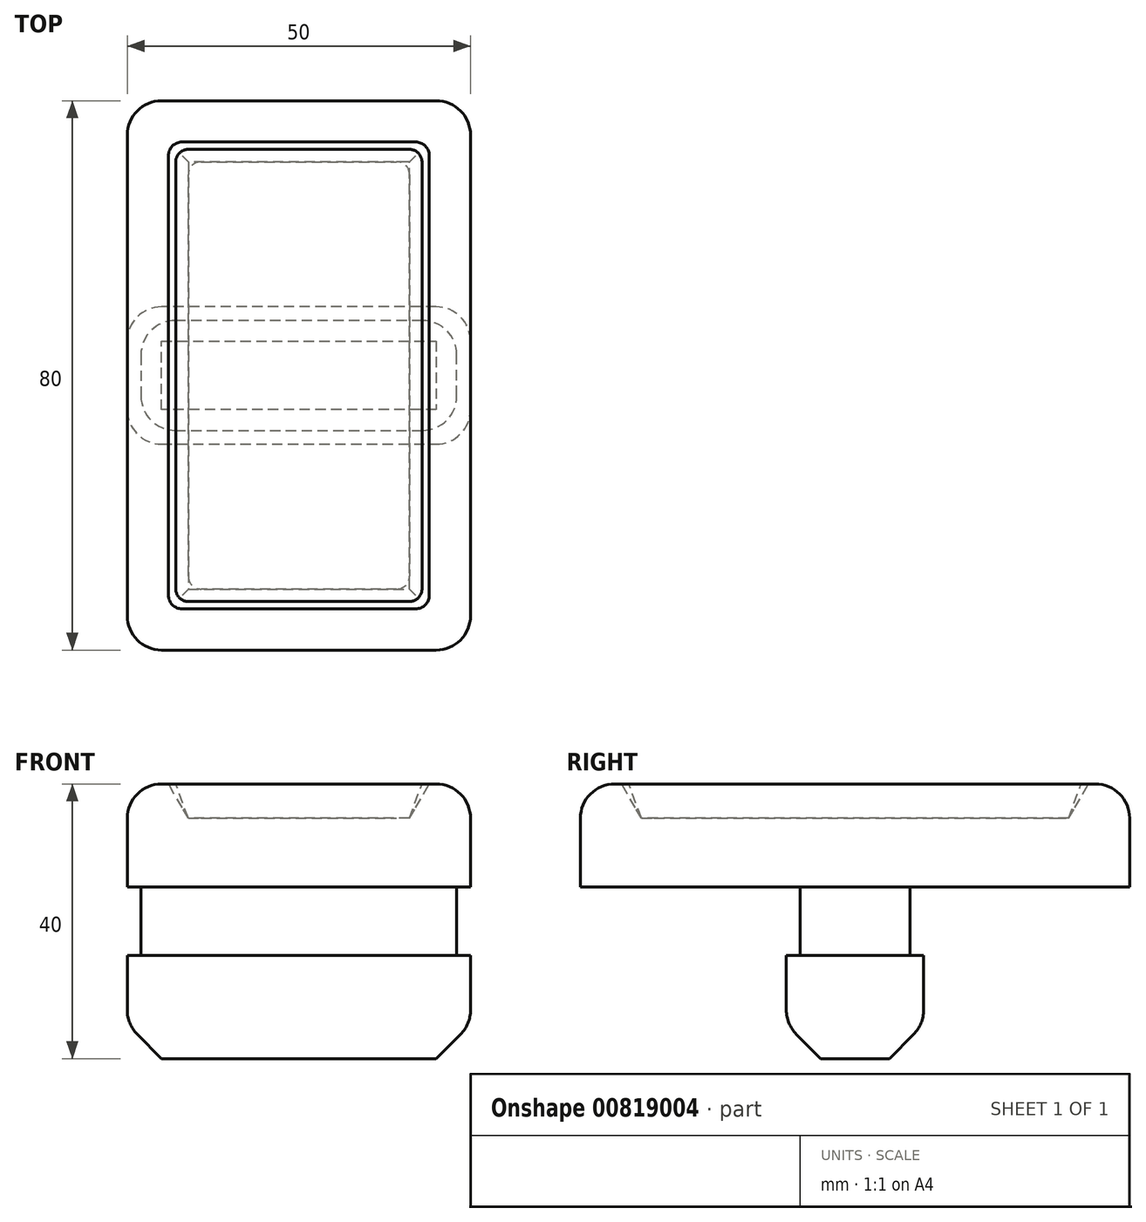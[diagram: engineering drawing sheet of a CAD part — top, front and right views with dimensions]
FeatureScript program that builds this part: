
annotation { "Feature Type Name" : "Feature", "Feature Type Description" : "" }
export const myFeature = defineFeature(function(context is Context, id is Id, definition is map)
    precondition{}
    {
        {
            var Q0;
            Q0=qCreatedBy(makeId("Top.planeOp"),FACE);
            var sketch = newSketch(context, id + "F0", { "sketchPlane" : qUnion([Q0])});
            skLineSegment(sketch, "E0.bottom", {"start": v(25, 40) * mm, "end": v(-25, 40) * mm});
            skLineSegment(sketch, "E0.top", {"start": v(25, -40) * mm, "end": v(-25, -40) * mm});
            skLineSegment(sketch, "E0.left", {"start": v(25, 40) * mm, "end": v(25, -40) * mm});
            skLineSegment(sketch, "E0.right", {"start": v(-25, 40) * mm, "end": v(-25, -40) * mm});
            skPoint(sketch, "E0.middle", {"position": v(0, 0) * mm});
            skSolve(sketch);
        }
        {
            var Q0;
            Q0=makeQuery(id+"F0.imprint","IMPRINT",FACE,{"disambiguationData":[TD([[makeQuery(id+"F0.imprint","IMPRINT",EDGE,{"derivedFrom":sQuery(id+"F0.wireOp",EDGE,"E0.bottom")}),1.0]])]});
            extrude(context, id + "F1", {"entities" : qUnion([Q0]), "depth" : 15 * mm, "offsetDistance" : 25 * mm});
        }
        {
            var Q0;
            Q0=makeQuery(id+"F1.opExtrude","CAP_EDGE",EDGE,{"disambiguationData":[OSD([sQuery(id+"F0.wireOp",EDGE,"E0.right")])],"isStart":false});
            var Q1;
            Q1=makeQuery(id+"F1.opExtrude","CAP_EDGE",EDGE,{"disambiguationData":[OSD([sQuery(id+"F0.wireOp",EDGE,"E0.top")])],"isStart":false});
            var Q2;
            Q2=makeQuery(id+"F1.opExtrude","CAP_EDGE",EDGE,{"disambiguationData":[OSD([sQuery(id+"F0.wireOp",EDGE,"E0.left")])],"isStart":false});
            var Q3;
            Q3=makeQuery(id+"F1.opExtrude","CAP_EDGE",EDGE,{"disambiguationData":[OSD([sQuery(id+"F0.wireOp",EDGE,"E0.bottom")])],"isStart":false});
            var Q4;
            Q4=makeQuery(id+"F1.opExtrude","SWEPT_EDGE",EDGE,{"disambiguationData":[OSD([sQuery(id+"F0.wireOp",EDGE,"E0.top"),sQuery(id+"F0.wireOp",EDGE,"E0.right")])]});
            var Q5;
            Q5=makeQuery(id+"F1.opExtrude","SWEPT_EDGE",EDGE,{"disambiguationData":[OSD([sQuery(id+"F0.wireOp",EDGE,"E0.top"),sQuery(id+"F0.wireOp",EDGE,"E0.left")])]});
            var Q6;
            Q6=makeQuery(id+"F1.opExtrude","SWEPT_EDGE",EDGE,{"disambiguationData":[OSD([sQuery(id+"F0.wireOp",EDGE,"E0.bottom"),sQuery(id+"F0.wireOp",EDGE,"E0.right")])]});
            var Q7;
            Q7=makeQuery(id+"F1.opExtrude","SWEPT_EDGE",EDGE,{"disambiguationData":[OSD([sQuery(id+"F0.wireOp",EDGE,"E0.bottom"),sQuery(id+"F0.wireOp",EDGE,"E0.left")])]});
            fillet(context, id + "F2", {"entities" : qUnion([Q0, Q1, Q2, Q3, Q4, Q5, Q6, Q7]), "radius" : 5 * mm, "tangentPropagation" : true, "allowEdgeOverflow" : false});
        }
        {
            var Q0;
            Q0=makeQuery(id+"F1.opExtrude","CAP_FACE",FACE,{"disambiguationData":[OSD([sQuery(id+"F0.wireOp",EDGE,"E0.bottom"),sQuery(id+"F0.wireOp",EDGE,"E0.top"),sQuery(id+"F0.wireOp",EDGE,"E0.left"),sQuery(id+"F0.wireOp",EDGE,"E0.right")])],"isStart":true});
            var sketch = newSketch(context, id + "F3", { "sketchPlane" : qUnion([Q0])});
            skLineSegment(sketch, "E1.0", {"start": v(-23, -3) * mm, "end": v(-23, 3) * mm});
            skLineSegment(sketch, "E1.1", {"start": v(-18, 8) * mm, "end": v(18, 8) * mm});
            skLineSegment(sketch, "E1.2", {"start": v(23, 3) * mm, "end": v(23, -3) * mm});
            skLineSegment(sketch, "E1.3", {"start": v(18, -8) * mm, "end": v(-18, -8) * mm});
            skPoint(sketch, "E2.visualSharp", {"position": v(-23, 8) * mm});
            skArc(sketch, "E2.filletArc", {"start": v(-18, 8) * mm, "mid": v(-21.54, 6.54) * mm, "end": v(-23, 3) * mm});
            skPoint(sketch, "E3.visualSharp", {"position": v(23, 8) * mm});
            skArc(sketch, "E3.filletArc", {"start": v(23, 3) * mm, "mid": v(21.54, 6.54) * mm, "end": v(18, 8) * mm});
            skPoint(sketch, "E4.visualSharp", {"position": v(23, -8) * mm});
            skArc(sketch, "E4.filletArc", {"start": v(18, -8) * mm, "mid": v(21.54, -6.54) * mm, "end": v(23, -3) * mm});
            skPoint(sketch, "E5.visualSharp", {"position": v(-23, -8) * mm});
            skArc(sketch, "E5.filletArc", {"start": v(-23, -3) * mm, "mid": v(-21.54, -6.54) * mm, "end": v(-18, -8) * mm});
            skSolve(sketch);
        }
        {
            var Q0;
            Q0=makeQuery(id+"F3.imprint","IMPRINT",FACE,{"disambiguationData":[TD([[makeQuery(id+"F3.imprint","IMPRINT",EDGE,{"derivedFrom":sQuery(id+"F3.wireOp",EDGE,"E1.0")}),-1.0]])]});
            extrude(context, id + "F4", {"entities" : qUnion([Q0]), "depth" : 10 * mm, "offsetDistance" : 25 * mm});
        }
        {
            var Q0;
            Q0=makeQuery(id+"F4.opExtrude","CAP_FACE",FACE,{"disambiguationData":[OSD([sQuery(id+"F3.wireOp",EDGE,"E1.0"),sQuery(id+"F3.wireOp",EDGE,"E1.1"),sQuery(id+"F3.wireOp",EDGE,"E1.2"),sQuery(id+"F3.wireOp",EDGE,"E1.3"),sQuery(id+"F3.wireOp",EDGE,"E2.filletArc"),sQuery(id+"F3.wireOp",EDGE,"E3.filletArc"),sQuery(id+"F3.wireOp",EDGE,"E4.filletArc"),sQuery(id+"F3.wireOp",EDGE,"E5.filletArc")])],"isStart":false});
            var sketch = newSketch(context, id + "F5", { "sketchPlane" : qUnion([Q0])});
            skLineSegment(sketch, "E6.0", {"start": v(25, -5) * mm, "end": v(25, 5) * mm});
            skLineSegment(sketch, "E6.1", {"start": v(-20, -10) * mm, "end": v(20, -10) * mm});
            skLineSegment(sketch, "E6.2", {"start": v(-25, 5) * mm, "end": v(-25, -5) * mm});
            skLineSegment(sketch, "E6.3", {"start": v(20, 10) * mm, "end": v(-20, 10) * mm});
            skPoint(sketch, "E7.visualSharp", {"position": v(-25, 10) * mm});
            skArc(sketch, "E7.filletArc", {"start": v(-20, 10) * mm, "mid": v(-23.54, 8.54) * mm, "end": v(-25, 5) * mm});
            skPoint(sketch, "E8.visualSharp", {"position": v(25, 10) * mm});
            skArc(sketch, "E8.filletArc", {"start": v(25, 5) * mm, "mid": v(23.54, 8.54) * mm, "end": v(20, 10) * mm});
            skPoint(sketch, "E9.visualSharp", {"position": v(25, -10) * mm});
            skArc(sketch, "E9.filletArc", {"start": v(20, -10) * mm, "mid": v(23.54, -8.54) * mm, "end": v(25, -5) * mm});
            skPoint(sketch, "E10.visualSharp", {"position": v(-25, -10) * mm});
            skArc(sketch, "E10.filletArc", {"start": v(-25, -5) * mm, "mid": v(-23.54, -8.54) * mm, "end": v(-20, -10) * mm});
            skSolve(sketch);
        }
        {
            var Q0;
            Q0 = qSketchRegion(id + "F5", true);
            extrude(context, id + "F6", {"entities" : qUnion([Q0]), "depth" : 15 * mm, "offsetDistance" : 25 * mm});
        }
        {
            var Q0;
            Q0=makeQuery(id+"F6.opExtrude","CAP_FACE",FACE,{"disambiguationData":[OSD([sQuery(id+"F5.wireOp",EDGE,"E6.0"),sQuery(id+"F5.wireOp",EDGE,"E6.1"),sQuery(id+"F5.wireOp",EDGE,"E6.2"),sQuery(id+"F5.wireOp",EDGE,"E6.3"),sQuery(id+"F5.wireOp",EDGE,"E7.filletArc"),sQuery(id+"F5.wireOp",EDGE,"E8.filletArc"),sQuery(id+"F5.wireOp",EDGE,"E9.filletArc"),sQuery(id+"F5.wireOp",EDGE,"E10.filletArc")])],"isStart":false});
            chamfer(context, id + "F7", {"entities" : qUnion([Q0]), "width" : 5 * mm, "tangentPropagation" : true});
        }
        {
            var Q0;
            {var subQ0=sQuery(id+"F5.wireOp",EDGE,"E6.0");Q0=makeQuery(id+"F7.opChamfer","BLEND_EDGE",EDGE,{"blendedFrom":[makeQuery(id+"F6.opExtrude","CAP_EDGE",EDGE,{"disambiguationData":[OSD([subQ0])],"isStart":false}),makeQuery(id+"F6.opExtrude","SWEPT_FACE",FACE,{"disambiguationData":[OSD([subQ0])]})],"blendedInto":[makeQuery(id+"F6.opExtrude","SWEPT_FACE",FACE,{"disambiguationData":[OSD([subQ0])]})]});}
            var Q1;
            {var subQ0=sQuery(id+"F5.wireOp",EDGE,"E9.filletArc");Q1=makeQuery(id+"F7.opChamfer","BLEND_EDGE",EDGE,{"blendedFrom":[makeQuery(id+"F6.opExtrude","CAP_EDGE",EDGE,{"disambiguationData":[OSD([subQ0])],"isStart":false}),makeQuery(id+"F6.opExtrude","SWEPT_FACE",FACE,{"disambiguationData":[OSD([subQ0])]})],"blendedInto":[makeQuery(id+"F6.opExtrude","SWEPT_FACE",FACE,{"disambiguationData":[OSD([subQ0])]})]});}
            var Q2;
            {var subQ0=sQuery(id+"F5.wireOp",EDGE,"E6.1");Q2=makeQuery(id+"F7.opChamfer","BLEND_EDGE",EDGE,{"blendedFrom":[makeQuery(id+"F6.opExtrude","CAP_EDGE",EDGE,{"disambiguationData":[OSD([subQ0])],"isStart":false}),makeQuery(id+"F6.opExtrude","SWEPT_FACE",FACE,{"disambiguationData":[OSD([subQ0])]})],"blendedInto":[makeQuery(id+"F6.opExtrude","SWEPT_FACE",FACE,{"disambiguationData":[OSD([subQ0])]})]});}
            fillet(context, id + "F8", {"entities" : qUnion([Q0, Q1, Q2]), "radius" : 5 * mm, "tangentPropagation" : true, "allowEdgeOverflow" : false});
        }
        {
            var Q0;
            Q0=makeQuery(id+"F1.opExtrude","CAP_FACE",FACE,{"disambiguationData":[OSD([sQuery(id+"F0.wireOp",EDGE,"E0.bottom"),sQuery(id+"F0.wireOp",EDGE,"E0.top"),sQuery(id+"F0.wireOp",EDGE,"E0.left"),sQuery(id+"F0.wireOp",EDGE,"E0.right")])],"isStart":false});
            var sketch = newSketch(context, id + "F9", { "sketchPlane" : qUnion([Q0])});
            skLineSegment(sketch, "E11.0", {"start": v(-19, 32) * mm, "end": v(-19, -32) * mm});
            skLineSegment(sketch, "E11.1", {"start": v(17, 34) * mm, "end": v(-17, 34) * mm});
            skLineSegment(sketch, "E11.2", {"start": v(19, -32) * mm, "end": v(19, 32) * mm});
            skLineSegment(sketch, "E11.3", {"start": v(-17, -34) * mm, "end": v(17, -34) * mm});
            skPoint(sketch, "E12.visualSharp", {"position": v(-19, -34) * mm});
            skArc(sketch, "E12.filletArc", {"start": v(-19, -32) * mm, "mid": v(-18.41, -33.41) * mm, "end": v(-17, -34) * mm});
            skPoint(sketch, "E13.visualSharp", {"position": v(-19, 34) * mm});
            skArc(sketch, "E13.filletArc", {"start": v(-17, 34) * mm, "mid": v(-18.41, 33.41) * mm, "end": v(-19, 32) * mm});
            skPoint(sketch, "E14.visualSharp", {"position": v(19, 34) * mm});
            skArc(sketch, "E14.filletArc", {"start": v(19, 32) * mm, "mid": v(18.41, 33.41) * mm, "end": v(17, 34) * mm});
            skPoint(sketch, "E15.visualSharp", {"position": v(19, -34) * mm});
            skArc(sketch, "E15.filletArc", {"start": v(17, -34) * mm, "mid": v(18.41, -33.41) * mm, "end": v(19, -32) * mm});
            skSolve(sketch);
        }
        {
            var Q0;
            Q0 = qSketchRegion(id + "F9", true);
            extrude(context, id + "F10", {"entities" : qUnion([Q0]), "operationType" : NewBodyOperationType.REMOVE, "oppositeDirection" : true, "depth" : 5 * mm, "offsetDistance" : 25 * mm, "hasDraft" : true, "draftAngle" : 30 * degree, "draftPullDirection" : true});
        }
        {
            var Q0;
            Q0=makeQuery(id+"F10.boolean.opBoolean","COPY",FACE,{"derivedFrom":makeQuery(id+"F10.opExtrude","CAP_FACE",FACE,{"disambiguationData":[OSD([sQuery(id+"F9.wireOp",EDGE,"E11.0"),sQuery(id+"F9.wireOp",EDGE,"E11.1"),sQuery(id+"F9.wireOp",EDGE,"E11.2"),sQuery(id+"F9.wireOp",EDGE,"E11.3"),sQuery(id+"F9.wireOp",EDGE,"E12.filletArc"),sQuery(id+"F9.wireOp",EDGE,"E13.filletArc"),sQuery(id+"F9.wireOp",EDGE,"E14.filletArc"),sQuery(id+"F9.wireOp",EDGE,"E15.filletArc")])],"isStart":false})});
            extrude(context, id + "F11", {"entities" : qUnion([Q0]), "depth" : 5 * mm, "offsetDistance" : 25 * mm, "hasDraft" : true, "draftAngle" : 20 * degree});
        }
        {
            var Q0;
            Q0=makeQuery(id+"F11.opExtrude","SWEPT_EDGE",EDGE,{"disambiguationData":[OSD([sQuery(id+"F9.wireOp",EDGE,"E11.0"),sQuery(id+"F9.wireOp",EDGE,"E11.3"),sQuery(id+"F9.wireOp",EDGE,"E12.filletArc")])]});
            var Q1;
            Q1=makeQuery(id+"F11.opExtrude","SWEPT_EDGE",EDGE,{"disambiguationData":[OSD([sQuery(id+"F9.wireOp",EDGE,"E11.0"),sQuery(id+"F9.wireOp",EDGE,"E11.1"),sQuery(id+"F9.wireOp",EDGE,"E13.filletArc")])]});
            var Q2;
            Q2=makeQuery(id+"F11.opExtrude","SWEPT_EDGE",EDGE,{"disambiguationData":[OSD([sQuery(id+"F9.wireOp",EDGE,"E11.2"),sQuery(id+"F9.wireOp",EDGE,"E11.3"),sQuery(id+"F9.wireOp",EDGE,"E15.filletArc")])]});
            var Q3;
            Q3=makeQuery(id+"F11.opExtrude","SWEPT_EDGE",EDGE,{"disambiguationData":[OSD([sQuery(id+"F9.wireOp",EDGE,"E11.1"),sQuery(id+"F9.wireOp",EDGE,"E11.2"),sQuery(id+"F9.wireOp",EDGE,"E14.filletArc")])]});
            fillet(context, id + "F12", {"entities" : qUnion([Q0, Q1, Q2, Q3]), "radius" : 2 * mm, "tangentPropagation" : true, "allowEdgeOverflow" : false});
        }
    });
